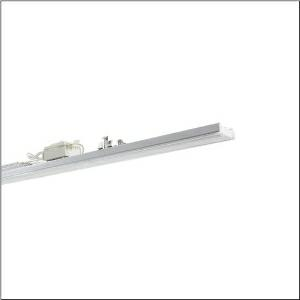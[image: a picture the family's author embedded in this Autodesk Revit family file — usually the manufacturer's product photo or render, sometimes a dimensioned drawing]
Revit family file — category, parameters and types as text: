
# Revit family: licross_r__21_recessed_mo_52tl12dn4axg3c_4f99
name_source: partatom
category: Lighting Fixtures
units: mm (PartAtom-declared; Revit-internal decimal feet)

## family parameters
Cut with Voids When Loaded = No
Host = Face
Light Source = No
Part Type = Normal
Room Calculation Point = No
Round Connector Dimension = Use Diameter
Shared = No

## types (1)
- --- (1 x LED, 950 lm, 6.7 W, 4000K)
    Apparent Load = 7 VA
    CIE Flux Codes = 72 92 99 100 100
    Color Rendering = 80
    Color Temperature = 4000K
    Default Elevation = 1800 mm
    Description = Licross® 21 Recessed MO, luminaire insert, of sheet steel, galvanised, coil coated, white, length: 1.500mm, width: 66mm, height: 67mm, LED rated luminous flux: 10.280lm, light colour: 840, control gear: DALI 2 (for two DALI lines), with plug, 6-pole, with phase selection, for trunking rail, 14-core, mains connection: 220..240V, AC, 50/60Hz, rated input power: 62W, internal wiring halogen-free, for emergency light function, for trunking rail, 14-core, converter,control gear: single battery element, battery: LiFePO4, 9Ah, primary optical cover: cover, of PMMA, light emission: direct distribution, primary light characteristic: symmetric, protection rating (complete): IP40, insulation class (complete): insulation class I (protective earthing), certification: CE, UKCA, protection symbol: D if used in an environment without relevant dust loads with corresponding accessories, impact resistance: IK06, permissible ambient temperature for indoor applications: +5..+35°C, standard: EN 60598-2-22, LABS conformity tested according to VDMA 24364:2018-05, reducing of maximum allowable ambient temperature of 5°C with ceiling mounting, corresponds to IFS (International Featured Standards) requirements for safety and quality in the food industry, packaging unit: 1 piece
    Height = 58 mm
    Lamp = 1 x LED
    Lamp Light Flux = 950 lm
    Lamp Power = 6.7 W
    Lamp count = 1
    Length = 1500 mm
    Luminous efficacy = 142 lm/W
    Manufacturer = Siteco
    ModVariant = No
    Model = 52TL12DN4AXG3C
    Mounting Place = Ceiling
    Mounting Type = Pendant
    Number of Poles = 1
    OnlyDefault = Yes
    Power Factor = 1
    Product Name = Licross® 21 Recessed MO
    Product group = luminaire insert | ceiling pendant
    ProductGroupID = 902
    Protection Class = Protection class I
    Protection Degree = IP 40
    RLX_Detail_Level = 1
    RLX_Emergency_Light_Flux = 0 lm
    RLX_Emergency_Type = 0
    RLX_Emergency_Type_DB = No
    RlxData = <blob elided: 25069 chars, md5=5ca8e8f3>
    Socket = socket
    Standby Power = 0 W
    System Light Flux = 950 lm
    System Power = 7 W
    Type Comments = : emergency light operation: 3 h
    Type Image = l_1296930.jpg
    URL = http://relux.com
    VarID = @adj_131533
    Voltage = 0 V
    Weight = 0.00 kg
    Width = 66 mm

## geometry (parser evidence)
native form markers: Blend x4, Sweep x10
no freeform markers — native parametric forms only
